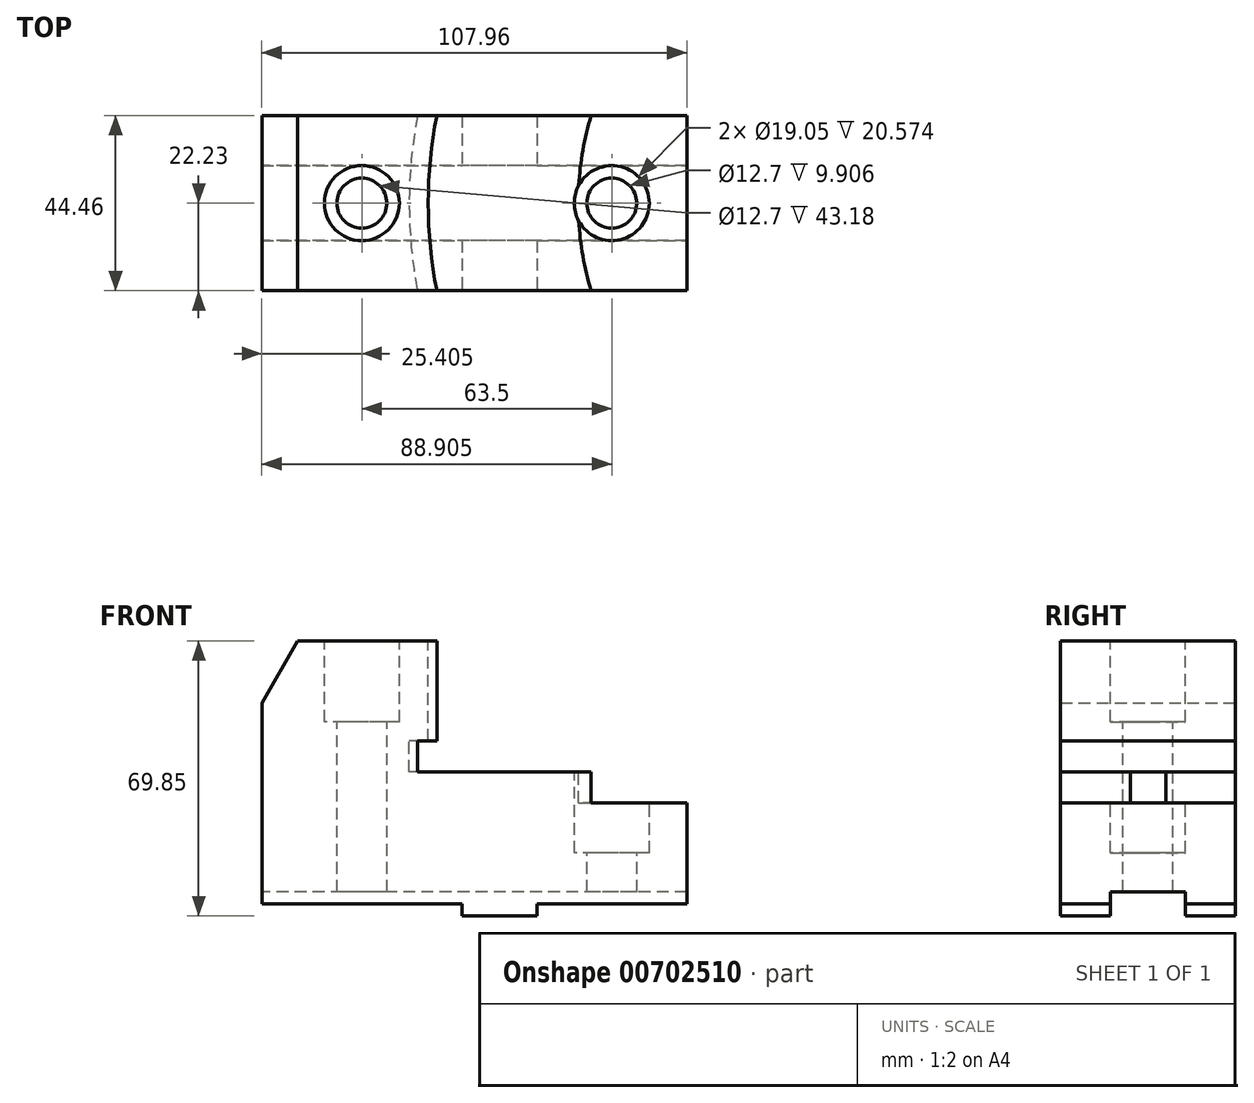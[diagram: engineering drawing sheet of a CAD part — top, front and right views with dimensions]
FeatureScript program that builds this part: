
annotation { "Feature Type Name" : "Feature", "Feature Type Description" : "" }
export const myFeature = defineFeature(function(context is Context, id is Id, definition is map)
    precondition{}
    {
        {
            var Q0;
            Q0=qCreatedBy(makeId("Front.planeOp"),FACE);
            var sketch = newSketch(context, id + "F0", { "sketchPlane" : qUnion([Q0])});
            skLineSegment(sketch, "E0.rect.bottom", {"start": v(53.98, 34.93) * mm, "end": v(-53.98, 34.93) * mm});
            skLineSegment(sketch, "E0.rect.top", {"start": v(53.98, -34.93) * mm, "end": v(-53.98, -34.93) * mm});
            skLineSegment(sketch, "E0.rect.left", {"start": v(53.98, 34.93) * mm, "end": v(53.98, -34.92) * mm});
            skLineSegment(sketch, "E0.rect.right", {"start": v(-53.98, 34.93) * mm, "end": v(-53.98, -34.93) * mm});
            skPoint(sketch, "E0.rect.middle", {"position": v(0, 0) * mm});
            skSolve(sketch);
        }
        {
            var Q0;
            Q0=qSketchRegion(id+"F0",true);
            extrude(context, id + "F1", {"entities" : qUnion([Q0]), "endBound" : BoundingType.SYMMETRIC, "depth" : 44.45 * mm});
        }
        {
            var Q0;
            Q0=qCreatedBy(makeId("Front.planeOp"),FACE);
            var sketch = newSketch(context, id + "F2", { "sketchPlane" : qUnion([Q0])});
            skLineSegment(sketch, "E1.bottom", {"start": v(-53.98, -34.93) * mm, "end": v(-3.17, -34.93) * mm});
            skLineSegment(sketch, "E1.top", {"start": v(-53.98, -31.88) * mm, "end": v(-3.18, -31.88) * mm});
            skLineSegment(sketch, "E1.left", {"start": v(-53.98, -34.93) * mm, "end": v(-53.98, -31.88) * mm});
            skLineSegment(sketch, "E1.right", {"start": v(-3.17, -34.93) * mm, "end": v(-3.17, -31.88) * mm});
            skLineSegment(sketch, "E2.bottom", {"start": v(15.88, -31.88) * mm, "end": v(53.98, -31.88) * mm});
            skLineSegment(sketch, "E2.top", {"start": v(15.88, -34.93) * mm, "end": v(53.98, -34.93) * mm});
            skLineSegment(sketch, "E2.left", {"start": v(15.88, -31.88) * mm, "end": v(15.88, -34.93) * mm});
            skLineSegment(sketch, "E2.right", {"start": v(53.98, -31.88) * mm, "end": v(53.98, -34.92) * mm});
            skSolve(sketch);
        }
        {
            var Q0;
            Q0=qSketchRegion(id+"F2",true);
            extrude(context, id + "F3", {"entities" : qUnion([Q0]), "operationType" : NewBodyOperationType.REMOVE, "endBound" : BoundingType.THROUGH_ALL, "oppositeDirection" : true, "depth" : 25.4 * mm, "hasSecondDirection" : true, "secondDirectionBound" : SecondDirectionBoundingType.THROUGH_ALL, "secondDirectionOppositeDirection" : false, "secondDirectionDepth" : 25.4 * mm});
        }
        {
            var Q0;
            Q0=qCreatedBy(makeId("Right.planeOp"),FACE);
            var sketch = newSketch(context, id + "F4", { "sketchPlane" : qUnion([Q0])});
            skLineSegment(sketch, "E3.bottom", {"start": v(-9.53, -28.83) * mm, "end": v(9.52, -28.83) * mm});
            skLineSegment(sketch, "E3.top", {"start": v(-9.52, -34.93) * mm, "end": v(9.52, -34.93) * mm});
            skLineSegment(sketch, "E3.left", {"start": v(-9.53, -28.83) * mm, "end": v(-9.53, -34.93) * mm});
            skLineSegment(sketch, "E3.right", {"start": v(9.53, -28.83) * mm, "end": v(9.53, -34.93) * mm});
            skSolve(sketch);
        }
        {
            var Q0;
            Q0=qSketchRegion(id+"F4",true);
            extrude(context, id + "F5", {"entities" : qUnion([Q0]), "operationType" : NewBodyOperationType.REMOVE, "endBound" : BoundingType.THROUGH_ALL, "depth" : 25.4 * mm, "hasSecondDirection" : true, "secondDirectionBound" : SecondDirectionBoundingType.THROUGH_ALL, "secondDirectionOppositeDirection" : true, "secondDirectionDepth" : 25.4 * mm});
        }
        {
            var Q0;
            Q0=makeQuery(id+"F1.opExtrude","SWEPT_FACE",FACE,{"disambiguationData":[OSD([sQuery(id+"F0.wireOp",EDGE,"E0.rect.bottom")])]});
            var sketch = newSketch(context, id + "F6", { "sketchPlane" : qUnion([Q0])});
            skCircle(sketch, "E4", {"center": v(102.6, 0) * mm, "radius": 114.3 * mm});
            skPoint(sketch, "E5", {"position": v(-9.52, 22.23) * mm});
            skSolve(sketch);
        }
        {
            var Q0;
            {var subQ1=sQuery(id+"F0.wireOp",EDGE,"E0.rect.bottom");var subQ6=makeQuery(id+"F1.opExtrude","SWEPT_EDGE",EDGE,{"disambiguationData":[OSD([subQ1,sQuery(id+"F0.wireOp",EDGE,"E0.rect.left")])]});Q0=makeQuery(id+"F6.imprint","IMPRINT",FACE,{"disambiguationData":[TD([[makeQuery(id+"F6.imprint","IMPRINT",EDGE,{"derivedFrom":subQ6}),1.0]])]});}
            extrude(context, id + "F7", {"entities" : qUnion([Q0]), "operationType" : NewBodyOperationType.REMOVE, "oppositeDirection" : true, "depth" : 25.4 * mm});
        }
        {
            var Q0;
            Q0=makeQuery(id+"F7.boolean.opBoolean","COPY",FACE,{"derivedFrom":makeQuery(id+"F7.opExtrude","CAP_FACE",FACE,{"disambiguationData":[OSD([sQuery(id+"F0.wireOp",EDGE,"E0.rect.bottom"),sQuery(id+"F0.wireOp",EDGE,"E0.rect.left"),sQuery(id+"F6.wireOp",EDGE,"E4")])],"isStart":false})});
            var sketch = newSketch(context, id + "F8", { "sketchPlane" : qUnion([Q0])});
            skCircle(sketch, "E6", {"center": v(102.6, 0) * mm, "radius": 119.13 * mm});
            skSolve(sketch);
        }
        {
            var Q0;
            Q0=qSketchRegion(id+"F8",true);
            extrude(context, id + "F9", {"entities" : qUnion([Q0]), "operationType" : NewBodyOperationType.REMOVE, "oppositeDirection" : true, "depth" : 7.87 * mm});
        }
        {
            var Q0;
            Q0=makeQuery(id+"F9.boolean.opBoolean","COPY",FACE,{"derivedFrom":makeQuery(id+"F9.opExtrude","CAP_FACE",FACE,{"disambiguationData":[OSD([sQuery(id+"F8.wireOp",EDGE,"E6")])],"isStart":false})});
            var sketch = newSketch(context, id + "F10", { "sketchPlane" : qUnion([Q0])});
            skCircle(sketch, "E7", {"center": v(102.6, 0) * mm, "radius": 76.2 * mm});
            skSolve(sketch);
        }
        {
            var Q0;
            Q0=qSketchRegion(id+"F10",true);
            extrude(context, id + "F11", {"entities" : qUnion([Q0]), "operationType" : NewBodyOperationType.REMOVE, "oppositeDirection" : true, "depth" : 7.87 * mm});
        }
        {
            var Q0;
            Q0=makeQuery(id+"F9.boolean.opBoolean","COPY",FACE,{"derivedFrom":makeQuery(id+"F9.opExtrude","CAP_FACE",FACE,{"disambiguationData":[OSD([sQuery(id+"F8.wireOp",EDGE,"E6")])],"isStart":false})});
            var sketch = newSketch(context, id + "F12", { "sketchPlane" : qUnion([Q0])});
            skLineSegment(sketch, "E8", {"start": v(34.92, -22.23) * mm, "end": v(34.92, 22.23) * mm});
            skPoint(sketch, "E9", {"position": v(34.92, 0) * mm});
            skSolve(sketch);
        }
        {
            var Q0;
            Q0=makeQuery(id+"F1.opExtrude","SWEPT_FACE",FACE,{"disambiguationData":[OSD([sQuery(id+"F0.wireOp",EDGE,"E0.rect.bottom")])]});
            var sketch = newSketch(context, id + "F13", { "sketchPlane" : qUnion([Q0])});
            skLineSegment(sketch, "E10", {"start": v(-28.57, -22.23) * mm, "end": v(-28.58, 22.23) * mm});
            skPoint(sketch, "E11", {"position": v(-28.58, 0) * mm});
            skSolve(sketch);
        }
        {
            var Q0;
            Q0=sQuery(id+"F13.wireOp",VERTEX,"E11");
            var Q1;
            Q1=makeQuery(id+"F1.opExtrude","SWEPT_BODY",BODY,{"disambiguationData":[OSD([sQuery(id+"F0.wireOp",EDGE,"E0.rect.bottom"),sQuery(id+"F0.wireOp",EDGE,"E0.rect.top"),sQuery(id+"F0.wireOp",EDGE,"E0.rect.left"),sQuery(id+"F0.wireOp",EDGE,"E0.rect.right")])]});
            hole(context, id + "F14", {"style" : HoleStyle.C_BORE, "holeDiameter" : 12.7 * mm, "cBoreDiameter" : 19.05 * mm, "cBoreDepth" : 20.57 * mm, "endStyle" : HoleEndStyle.THROUGH, "locations" : qUnion([Q0]), "scope" : qUnion([Q1])});
        }
        {
            var Q0;
            Q0=sQuery(id+"F12.wireOp",VERTEX,"E9");
            var Q1;
            Q1=makeQuery(id+"F1.opExtrude","SWEPT_BODY",BODY,{"disambiguationData":[OSD([sQuery(id+"F0.wireOp",EDGE,"E0.rect.bottom"),sQuery(id+"F0.wireOp",EDGE,"E0.rect.top"),sQuery(id+"F0.wireOp",EDGE,"E0.rect.left"),sQuery(id+"F0.wireOp",EDGE,"E0.rect.right")])]});
            hole(context, id + "F15", {"style" : HoleStyle.SIMPLE, "holeDiameter" : 12.7 * mm, "endStyle" : HoleEndStyle.THROUGH, "locations" : qUnion([Q0]), "scope" : qUnion([Q1])});
        }
        {
            var Q0;
            Q0=makeQuery(id+"F9.boolean.opBoolean","COPY",FACE,{"derivedFrom":makeQuery(id+"F9.opExtrude","CAP_FACE",FACE,{"disambiguationData":[OSD([sQuery(id+"F8.wireOp",EDGE,"E6")])],"isStart":false})});
            var sketch = newSketch(context, id + "F16", { "sketchPlane" : qUnion([Q0])});
            skCircle(sketch, "E12", {"center": v(34.92, 0) * mm, "radius": 9.53 * mm});
            skSolve(sketch);
        }
        {
            var Q0;
            Q0=qSketchRegion(id+"F16",true);
            extrude(context, id + "F17", {"entities" : qUnion([Q0]), "operationType" : NewBodyOperationType.REMOVE, "oppositeDirection" : true, "depth" : 20.57 * mm});
        }
        {
            var Q0;
            Q0=makeQuery(id+"F1.opExtrude","SWEPT_EDGE",EDGE,{"disambiguationData":[OSD([sQuery(id+"F0.wireOp",EDGE,"E0.rect.bottom"),sQuery(id+"F0.wireOp",EDGE,"E0.rect.right")])]});
            chamfer(context, id + "F18", {"entities" : qUnion([Q0]), "chamferType" : ChamferType.OFFSET_ANGLE, "width" : 15.75 * mm, "oppositeDirection" : false, "angle" : 30 * degree, "tangentPropagation" : true});
        }
    });
